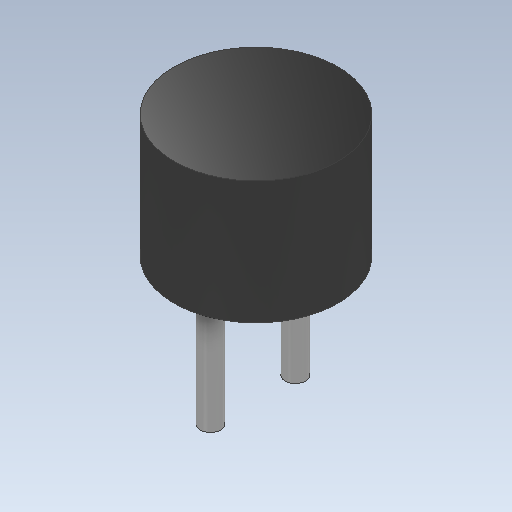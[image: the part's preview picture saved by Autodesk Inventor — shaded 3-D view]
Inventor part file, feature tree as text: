
AUTODESK INVENTOR PART (.ipt)
format: ipt  version: 2021 (Build 250183000, 183)  size: 107,520 bytes
history: native  units: mm
features: extrude x2, sketch x2
ambient origin geometry x8: Origin, YZ Plane, XZ Plane, XY Plane, X Axis, Y Axis, Z Axis, Center Point
bodies: Solid1 (feature_tree)
feature tree (4):
  extrude  "Extrusion1"  Depth=6.0mm TaperAngle=0.0deg
  extrude  "Extrusion2"  Depth=6.0mm
  sketch  "Sketch1"  dims[d0=8.0mm d1=6.0mm d2=0.0mm]
  sketch  "Sketch2"  dims[d3=1.0mm d4=1.0mm d5=6.0mm d6=0.0mm]
